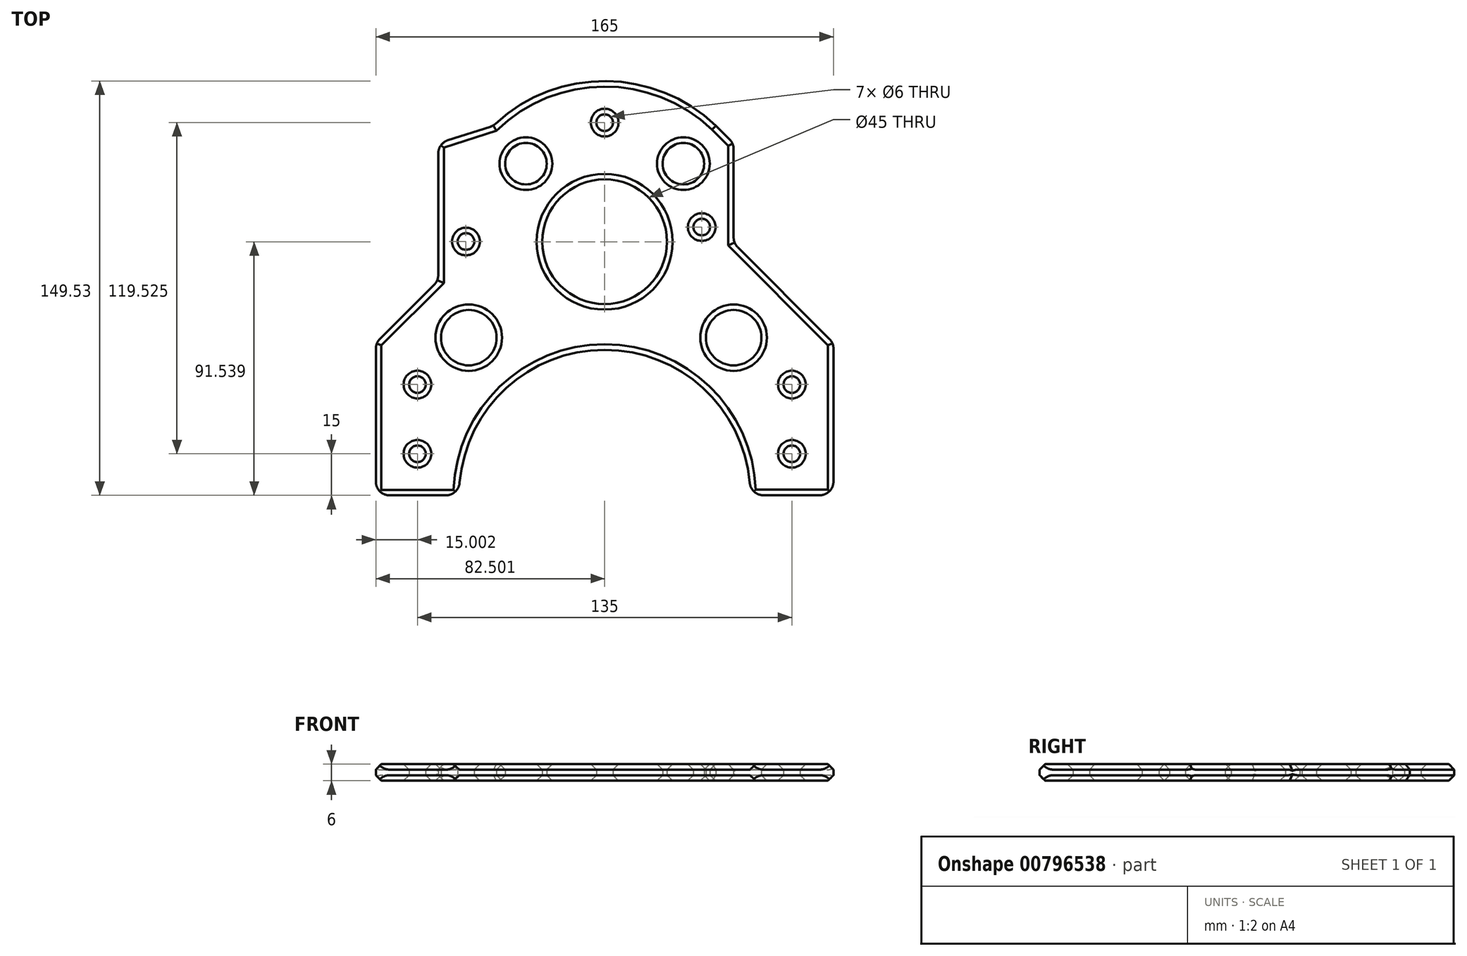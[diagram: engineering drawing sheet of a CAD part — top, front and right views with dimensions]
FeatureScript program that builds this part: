
annotation { "Feature Type Name" : "Feature", "Feature Type Description" : "" }
export const myFeature = defineFeature(function(context is Context, id is Id, definition is map)
    precondition{}
    {
        {
            var Q0;
            Q0=qCreatedBy(makeId("Top.planeOp"),FACE);
            var sketch = newSketch(context, id + "F0", { "sketchPlane" : qUnion([Q0])});
            skArc(sketch, "E0", {"start": v(92.61, -67.9) * mm, "mid": v(40.1, -15.4) * mm, "end": v(-12.39, -67.92) * mm});
            skLineSegment(sketch, "E1", {"start": v(122.61, -67.9) * mm, "end": v(122.61, -12.9) * mm});
            skLineSegment(sketch, "E2", {"start": v(122.61, -12.9) * mm, "end": v(86.61, -12.9) * mm});
            skLineSegment(sketch, "E3", {"start": v(86.61, -12.9) * mm, "end": v(86.61, 59.1) * mm});
            skLineSegment(sketch, "E4", {"start": v(-19.89, 59.1) * mm, "end": v(-19.89, -12.92) * mm});
            skLineSegment(sketch, "E5", {"start": v(-19.89, -12.92) * mm, "end": v(-42.39, -12.92) * mm});
            skLineSegment(sketch, "E6", {"start": v(-42.39, -12.92) * mm, "end": v(-42.39, -67.92) * mm});
            skLineSegment(sketch, "E7", {"start": v(-42.39, -67.92) * mm, "end": v(-12.39, -67.92) * mm});
            skLineSegment(sketch, "E8", {"start": v(92.61, -67.9) * mm, "end": v(122.61, -67.9) * mm});
            skArc(sketch, "E9", {"start": v(80.22, 65.5) * mm, "mid": v(40.11, 81.6) * mm, "end": v(0, 65.5) * mm});
            skCircle(sketch, "E10", {"center": v(40.11, 66.6) * mm, "radius": 3 * mm});
            skCircle(sketch, "E11", {"center": v(75.11, 28.9) * mm, "radius": 3 * mm});
            skCircle(sketch, "E12", {"center": v(-9.89, 23.7) * mm, "radius": 3 * mm});
            skCircle(sketch, "E13", {"center": v(-27.39, -27.92) * mm, "radius": 3 * mm});
            skCircle(sketch, "E14", {"center": v(-27.39, -52.92) * mm, "radius": 3 * mm});
            skCircle(sketch, "E15", {"center": v(107.61, -27.92) * mm, "radius": 3 * mm});
            skCircle(sketch, "E16", {"center": v(107.61, -52.92) * mm, "radius": 3 * mm});
            skLineSegment(sketch, "E17", {"start": v(80.22, 65.5) * mm, "end": v(86.61, 59.1) * mm});
            skLineSegment(sketch, "E18", {"start": v(0, 65.5) * mm, "end": v(-19.89, 59.1) * mm});
            skLineSegment(sketch, "E19", {"start": v(40.11, 81.6) * mm, "end": v(40.11, -15.4) * mm});
            skLineSegment(sketch, "E20", {"start": v(122.61, -12.9) * mm, "end": v(86.61, 23.1) * mm});
            skLineSegment(sketch, "E21", {"start": v(-42.39, -12.92) * mm, "end": v(-19.89, 9.58) * mm});
            skCircle(sketch, "E22", {"center": v(40.11, 23.62) * mm, "radius": 22.5 * mm});
            skCircle(sketch, "E23", {"center": v(11.72, 51.8) * mm, "radius": 7.5 * mm});
            skCircle(sketch, "E24", {"center": v(68.5, 51.8) * mm, "radius": 7.5 * mm});
            skCircle(sketch, "E25", {"center": v(86.61, -11) * mm, "radius": 10 * mm});
            skCircle(sketch, "E26", {"center": v(-8.89, -11) * mm, "radius": 10 * mm});
            skSolve(sketch);
        }
        {
            var Q0;
            Q0 = qSketchRegion(id + "F0", true);
            extrude(context, id + "F1", {"entities" : qUnion([Q0]), "depth" : 6 * mm, "offsetDistance" : 25 * mm});
        }
        {
            var Q0;
            Q0=makeQuery(id+"F1.opExtrude","CAP_FACE",FACE,{"disambiguationData":[OSD([sQuery(id+"F0.wireOp",EDGE,"E0"),sQuery(id+"F0.wireOp",EDGE,"E1"),sQuery(id+"F0.wireOp",EDGE,"E3"),sQuery(id+"F0.wireOp",EDGE,"E4"),sQuery(id+"F0.wireOp",EDGE,"E6"),sQuery(id+"F0.wireOp",EDGE,"E7"),sQuery(id+"F0.wireOp",EDGE,"E8"),sQuery(id+"F0.wireOp",EDGE,"E9"),sQuery(id+"F0.wireOp",EDGE,"E10"),sQuery(id+"F0.wireOp",EDGE,"E11"),sQuery(id+"F0.wireOp",EDGE,"E12"),sQuery(id+"F0.wireOp",EDGE,"E13"),sQuery(id+"F0.wireOp",EDGE,"E14"),sQuery(id+"F0.wireOp",EDGE,"E15"),sQuery(id+"F0.wireOp",EDGE,"E16"),sQuery(id+"F0.wireOp",EDGE,"E17"),sQuery(id+"F0.wireOp",EDGE,"E18"),sQuery(id+"F0.wireOp",EDGE,"E20"),sQuery(id+"F0.wireOp",EDGE,"E21")])],"isStart":false});
            var Q1;
            Q1=makeQuery(id+"F1.opExtrude","CAP_FACE",FACE,{"disambiguationData":[OSD([sQuery(id+"F0.wireOp",EDGE,"E0"),sQuery(id+"F0.wireOp",EDGE,"E1"),sQuery(id+"F0.wireOp",EDGE,"E3"),sQuery(id+"F0.wireOp",EDGE,"E4"),sQuery(id+"F0.wireOp",EDGE,"E6"),sQuery(id+"F0.wireOp",EDGE,"E7"),sQuery(id+"F0.wireOp",EDGE,"E8"),sQuery(id+"F0.wireOp",EDGE,"E9"),sQuery(id+"F0.wireOp",EDGE,"E10"),sQuery(id+"F0.wireOp",EDGE,"E11"),sQuery(id+"F0.wireOp",EDGE,"E12"),sQuery(id+"F0.wireOp",EDGE,"E13"),sQuery(id+"F0.wireOp",EDGE,"E14"),sQuery(id+"F0.wireOp",EDGE,"E15"),sQuery(id+"F0.wireOp",EDGE,"E16"),sQuery(id+"F0.wireOp",EDGE,"E17"),sQuery(id+"F0.wireOp",EDGE,"E18"),sQuery(id+"F0.wireOp",EDGE,"E20"),sQuery(id+"F0.wireOp",EDGE,"E21")])],"isStart":true});
            chamfer(context, id + "F2", {"entities" : qUnion([Q0, Q1]), "width" : 2 * mm, "tangentPropagation" : true});
        }
        {
            var Q0;
            Q0=makeQuery(id+"F1.opExtrude","SWEPT_EDGE",EDGE,{"disambiguationData":[OSD([sQuery(id+"F0.wireOp",EDGE,"E0"),sQuery(id+"F0.wireOp",EDGE,"E7")])]});
            var Q1;
            Q1=makeQuery(id+"F1.opExtrude","SWEPT_EDGE",EDGE,{"disambiguationData":[OSD([sQuery(id+"F0.wireOp",EDGE,"E6"),sQuery(id+"F0.wireOp",EDGE,"E7")])]});
            var Q2;
            Q2=makeQuery(id+"F1.opExtrude","SWEPT_EDGE",EDGE,{"disambiguationData":[OSD([sQuery(id+"F0.wireOp",EDGE,"E0"),sQuery(id+"F0.wireOp",EDGE,"E8")])]});
            var Q3;
            Q3=makeQuery(id+"F1.opExtrude","SWEPT_EDGE",EDGE,{"disambiguationData":[OSD([sQuery(id+"F0.wireOp",EDGE,"E1"),sQuery(id+"F0.wireOp",EDGE,"E8")])]});
            var Q4;
            Q4=makeQuery(id+"F1.opExtrude","SWEPT_EDGE",EDGE,{"disambiguationData":[OSD([sQuery(id+"F0.wireOp",EDGE,"E1"),sQuery(id+"F0.wireOp",EDGE,"E2"),sQuery(id+"F0.wireOp",EDGE,"E20")])]});
            var Q5;
            Q5=makeQuery(id+"F1.opExtrude","SWEPT_EDGE",EDGE,{"disambiguationData":[OSD([sQuery(id+"F0.wireOp",EDGE,"E5"),sQuery(id+"F0.wireOp",EDGE,"E6"),sQuery(id+"F0.wireOp",EDGE,"E21")])]});
            var Q6;
            Q6=makeQuery(id+"F1.opExtrude","SWEPT_EDGE",EDGE,{"disambiguationData":[OSD([sQuery(id+"F0.wireOp",EDGE,"E4"),sQuery(id+"F0.wireOp",EDGE,"E21")])]});
            var Q7;
            Q7=makeQuery(id+"F1.opExtrude","SWEPT_EDGE",EDGE,{"disambiguationData":[OSD([sQuery(id+"F0.wireOp",EDGE,"E4"),sQuery(id+"F0.wireOp",EDGE,"E18")])]});
            var Q8;
            Q8=makeQuery(id+"F1.opExtrude","SWEPT_EDGE",EDGE,{"disambiguationData":[OSD([sQuery(id+"F0.wireOp",EDGE,"E9"),sQuery(id+"F0.wireOp",EDGE,"E18")])]});
            var Q9;
            Q9=makeQuery(id+"F1.opExtrude","SWEPT_EDGE",EDGE,{"disambiguationData":[OSD([sQuery(id+"F0.wireOp",EDGE,"E3"),sQuery(id+"F0.wireOp",EDGE,"E17")])]});
            var Q10;
            Q10=makeQuery(id+"F1.opExtrude","SWEPT_EDGE",EDGE,{"disambiguationData":[OSD([sQuery(id+"F0.wireOp",EDGE,"E3"),sQuery(id+"F0.wireOp",EDGE,"E20")])]});
            fillet(context, id + "F3", {"entities" : qUnion([Q0, Q1, Q2, Q3, Q4, Q5, Q6, Q7, Q8, Q9, Q10]), "radius" : 5 * mm, "tangentPropagation" : true, "allowEdgeOverflow" : false});
        }
    });
